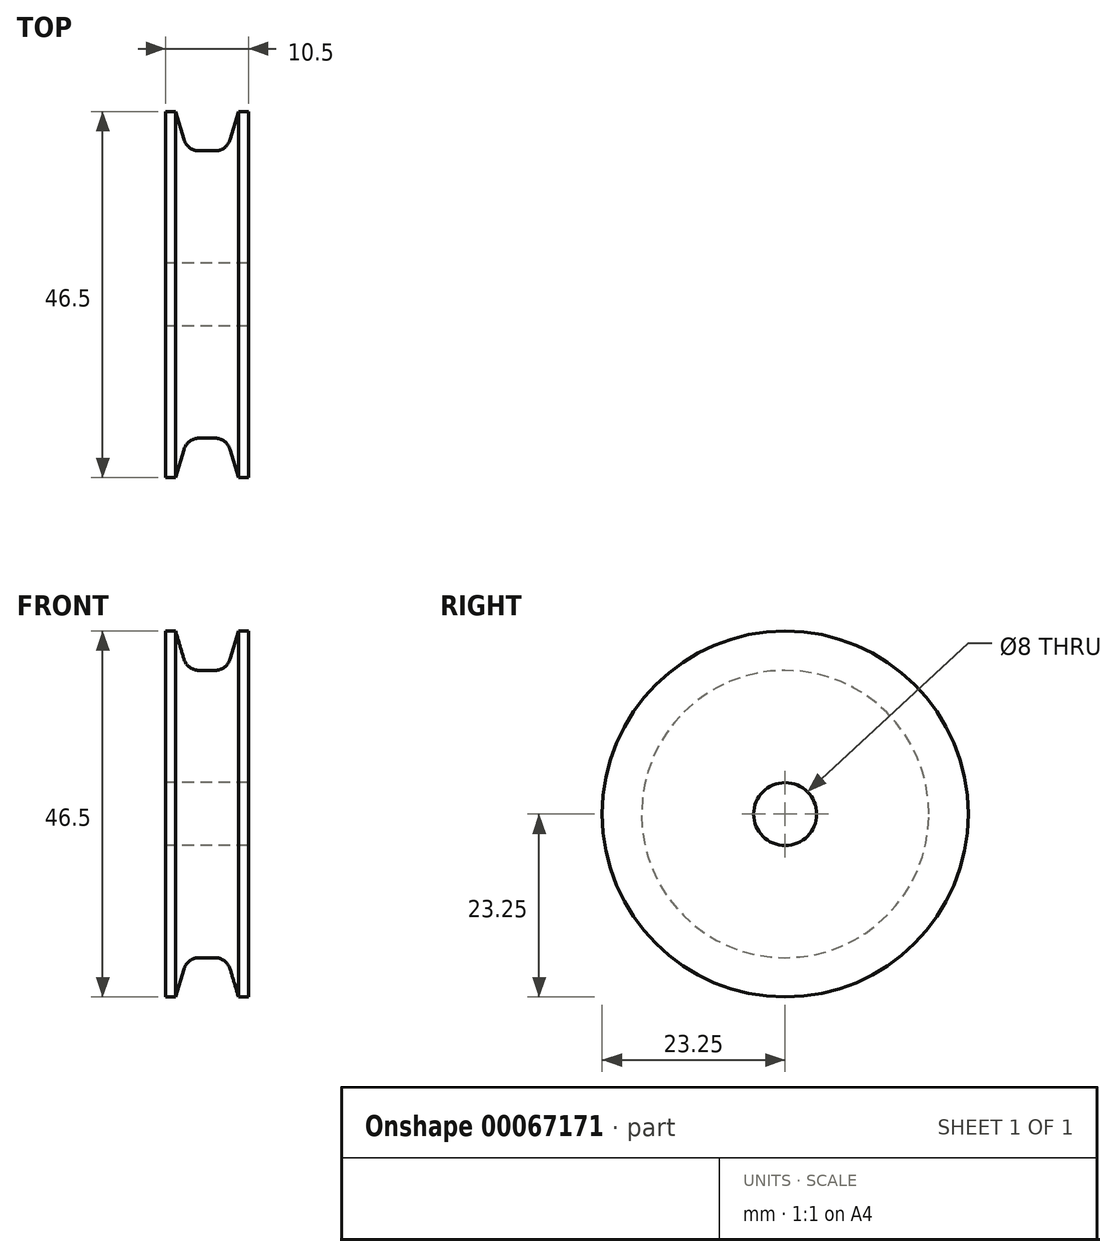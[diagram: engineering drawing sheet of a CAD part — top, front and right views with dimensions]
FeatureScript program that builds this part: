
annotation { "Feature Type Name" : "Feature", "Feature Type Description" : "" }
export const myFeature = defineFeature(function(context is Context, id is Id, definition is map)
    precondition{}
    {
        {
            var Q0;
            Q0=qCreatedBy(makeId("Front.planeOp"),FACE);
            var sketch = newSketch(context, id + "F0", { "sketchPlane" : qUnion([Q0])});
            skLineSegment(sketch, "E0", {"start": v(-7.12, 0) * mm, "end": v(8.56, 0) * mm, "construction": true});
            skLineSegment(sketch, "E1", {"start": v(0, 4) * mm, "end": v(5.25, 4) * mm});
            skLineSegment(sketch, "E2", {"start": v(5.25, 4) * mm, "end": v(5.25, 23.25) * mm});
            skLineSegment(sketch, "E3", {"start": v(5.25, 23.25) * mm, "end": v(4, 23.25) * mm});
            skLineSegment(sketch, "E4", {"start": v(4, 23.25) * mm, "end": v(2.5, 18.25) * mm});
            skLineSegment(sketch, "E5", {"start": v(2.5, 18.25) * mm, "end": v(0, 18.25) * mm});
            skLineSegment(sketch, "E6", {"start": v(0, 18.25) * mm, "end": v(0, 4) * mm});
            skLineSegment(sketch, "E7", {"start": v(0, 37.46) * mm, "end": v(0, 0) * mm, "construction": true});
            skLineSegment(sketch, "E8.MirrorCS", {"start": v(-5.25, 23.25) * mm, "end": v(-4, 23.25) * mm});
            skLineSegment(sketch, "E9.MirrorCS", {"start": v(-4, 23.25) * mm, "end": v(-2.5, 18.25) * mm});
            skLineSegment(sketch, "E10.MirrorCS", {"start": v(-5.25, 4) * mm, "end": v(-5.25, 23.25) * mm});
            skLineSegment(sketch, "E11.MirrorCS", {"start": v(0, 4) * mm, "end": v(-5.25, 4) * mm});
            skLineSegment(sketch, "E12.MirrorCS", {"start": v(-2.5, 18.25) * mm, "end": v(0, 18.25) * mm});
            skSolve(sketch);
        }
        {
            var Q0;
            Q0=qSketchRegion(id+"F0",true);
            var Q1;
            Q1=sQuery(id+"F0.wireOp",EDGE,"E0");
            revolve(context, id + "F1", {"entities" : qUnion([Q0]), "axis" : qUnion([Q1]), "revolveType" : RevolveType.FULL});
        }
        {
            var Q0;
            Q0=makeQuery(id+"F1.opRevolve","SWEPT_EDGE",EDGE,{"disambiguationData":[OSD([sQuery(id+"F0.wireOp",EDGE,"E4"),sQuery(id+"F0.wireOp",EDGE,"E5")])]});
            fillet(context, id + "F2", {"entities" : qUnion([Q0]), "radius" : 2 * mm, "tangentPropagation" : true, "allowEdgeOverflow" : false});
        }
        {
            var Q0;
            Q0=makeQuery(id+"F1.opRevolve","SWEPT_EDGE",EDGE,{"disambiguationData":[OSD([sQuery(id+"F0.wireOp",EDGE,"E12.MirrorCS"),sQuery(id+"F0.wireOp",EDGE,"E9.MirrorCS")])]});
            fillet(context, id + "F3", {"entities" : qUnion([Q0]), "radius" : 2 * mm, "tangentPropagation" : true, "allowEdgeOverflow" : false});
        }
    });
